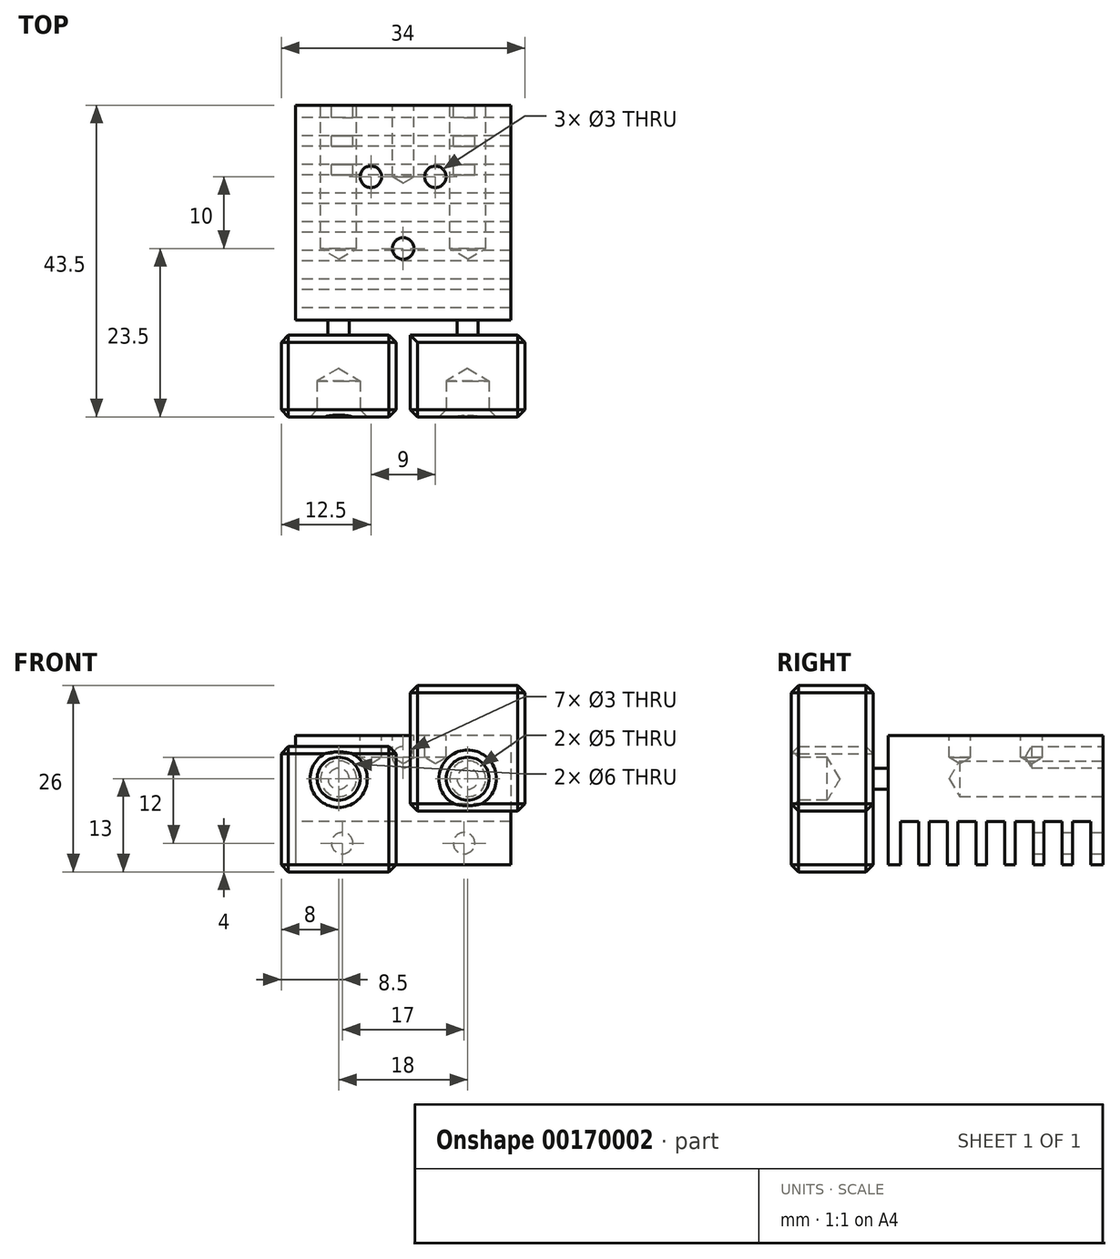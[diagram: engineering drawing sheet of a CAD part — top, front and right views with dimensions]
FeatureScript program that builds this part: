
annotation { "Feature Type Name" : "Feature", "Feature Type Description" : "" }
export const myFeature = defineFeature(function(context is Context, id is Id, definition is map)
    precondition{}
    {
        {
            var Q0;
            Q0=qCreatedBy(makeId("Top.planeOp"),FACE);
            var sketch = newSketch(context, id + "F0", { "sketchPlane" : qUnion([Q0])});
            skLineSegment(sketch, "E0.bottom", {"start": v(15, -15) * mm, "end": v(-15, -15) * mm});
            skLineSegment(sketch, "E0.top", {"start": v(15, 15) * mm, "end": v(-15, 15) * mm});
            skLineSegment(sketch, "E0.left", {"start": v(15, -15) * mm, "end": v(15, 15) * mm});
            skLineSegment(sketch, "E0.right", {"start": v(-15, -15) * mm, "end": v(-15, 15) * mm});
            skPoint(sketch, "E0.middle", {"position": v(0, 0) * mm});
            skSolve(sketch);
        }
        {
            var Q0;
            Q0=makeQuery(id+"F0.imprint","IMPRINT",FACE,{"disambiguationData":[TD([[makeQuery(id+"F0.imprint","IMPRINT",EDGE,{"derivedFrom":sQuery(id+"F0.wireOp",EDGE,"E0.bottom")}),-1.0]])]});
            extrude(context, id + "F6", {"entities" : qUnion([Q0]), "depth" : 18 * mm});
        }
        {
            var Q0;
            Q0=makeQuery(id+"F6.opExtrude","SWEPT_FACE",FACE,{"disambiguationData":[OSD([sQuery(id+"F0.wireOp",EDGE,"E0.top")])]});
            var sketch = newSketch(context, id + "F7", { "sketchPlane" : qUnion([Q0])});
            skPoint(sketch, "E1", {"position": v(-8.5, 3) * mm});
            skPoint(sketch, "E2", {"position": v(8.5, 3) * mm});
            skPoint(sketch, "E3", {"position": v(-9, 12) * mm});
            skPoint(sketch, "E4", {"position": v(9, 12) * mm});
            skPoint(sketch, "E5", {"position": v(0, 15) * mm});
            skSolve(sketch);
        }
        {
            var Q0;
            Q0=sQuery(id+"F7.wireOp",VERTEX,"E3");
            var Q1;
            Q1=sQuery(id+"F7.wireOp",VERTEX,"E4");
            var Q2;
            Q2=makeQuery(id+"F6.opExtrude","SWEPT_BODY",BODY,{"disambiguationData":[OSD([sQuery(id+"F0.wireOp",EDGE,"E0.bottom"),sQuery(id+"F0.wireOp",EDGE,"E0.top"),sQuery(id+"F0.wireOp",EDGE,"E0.left"),sQuery(id+"F0.wireOp",EDGE,"E0.right")])]});
            hole(context, id + "F1", {"style" : HoleStyle.SIMPLE, "endStyle" : HoleEndStyle.BLIND, "holeDiameter" : 5 * mm, "holeDepth" : 20 * mm, "locations" : qUnion([Q0, Q1]), "scope" : qUnion([Q2])});
        }
        {
            var Q0;
            Q0=makeQuery(id+"F6.opExtrude","CAP_FACE",FACE,{"disambiguationData":[OSD([sQuery(id+"F0.wireOp",EDGE,"E0.bottom"),sQuery(id+"F0.wireOp",EDGE,"E0.top"),sQuery(id+"F0.wireOp",EDGE,"E0.left"),sQuery(id+"F0.wireOp",EDGE,"E0.right")])],"isStart":true});
            var sketch = newSketch(context, id + "F8", { "sketchPlane" : qUnion([Q0])});
            skLineSegment(sketch, "E6.bottom", {"start": v(15, -13.25) * mm, "end": v(-15.01, -13.25) * mm});
            skLineSegment(sketch, "E6.top", {"start": v(15, -10.75) * mm, "end": v(-15.01, -10.75) * mm});
            skLineSegment(sketch, "E6.left", {"start": v(15, -13.25) * mm, "end": v(15, -10.75) * mm});
            skLineSegment(sketch, "E6.right", {"start": v(-15.01, -13.25) * mm, "end": v(-15.01, -10.75) * mm});
            skLineSegment(sketch, "E7.0.1.0", {"start": v(15, -9.25) * mm, "end": v(15, -6.75) * mm});
            skLineSegment(sketch, "E7.0.1.1", {"start": v(-15.01, -9.25) * mm, "end": v(-15.01, -6.75) * mm});
            skLineSegment(sketch, "E7.0.1.2", {"start": v(15, -9.25) * mm, "end": v(-15.01, -9.25) * mm});
            skLineSegment(sketch, "E7.0.1.3", {"start": v(15, -6.75) * mm, "end": v(-15.01, -6.75) * mm});
            skLineSegment(sketch, "E7.0.2.0", {"start": v(15, -5.25) * mm, "end": v(15, -2.75) * mm});
            skLineSegment(sketch, "E7.0.2.1", {"start": v(-15.01, -5.25) * mm, "end": v(-15.01, -2.75) * mm});
            skLineSegment(sketch, "E7.0.2.2", {"start": v(15, -5.25) * mm, "end": v(-15.01, -5.25) * mm});
            skLineSegment(sketch, "E7.0.2.3", {"start": v(15, -2.75) * mm, "end": v(-15.01, -2.75) * mm});
            skLineSegment(sketch, "E7.0.3.0", {"start": v(15, -1.25) * mm, "end": v(15, 1.25) * mm});
            skLineSegment(sketch, "E7.0.3.1", {"start": v(-15.01, -1.25) * mm, "end": v(-15.01, 1.25) * mm});
            skLineSegment(sketch, "E7.0.3.2", {"start": v(15, -1.25) * mm, "end": v(-15.01, -1.25) * mm});
            skLineSegment(sketch, "E7.0.3.3", {"start": v(15, 1.25) * mm, "end": v(-15.01, 1.25) * mm});
            skLineSegment(sketch, "E7.0.4.0", {"start": v(15, 2.75) * mm, "end": v(15, 5.25) * mm});
            skLineSegment(sketch, "E7.0.4.1", {"start": v(-15.01, 2.75) * mm, "end": v(-15.01, 5.25) * mm});
            skLineSegment(sketch, "E7.0.4.2", {"start": v(15, 2.75) * mm, "end": v(-15.01, 2.75) * mm});
            skLineSegment(sketch, "E7.0.4.3", {"start": v(15, 5.25) * mm, "end": v(-15.01, 5.25) * mm});
            skLineSegment(sketch, "E7.0.5.0", {"start": v(15, 6.75) * mm, "end": v(15, 9.25) * mm});
            skLineSegment(sketch, "E7.0.5.1", {"start": v(-15.01, 6.75) * mm, "end": v(-15.01, 9.25) * mm});
            skLineSegment(sketch, "E7.0.5.2", {"start": v(15, 6.75) * mm, "end": v(-15.01, 6.75) * mm});
            skLineSegment(sketch, "E7.0.5.3", {"start": v(15, 9.25) * mm, "end": v(-15.01, 9.25) * mm});
            skLineSegment(sketch, "E7.0.6.0", {"start": v(15, 10.75) * mm, "end": v(15, 13.25) * mm});
            skLineSegment(sketch, "E7.0.6.1", {"start": v(-15.01, 10.75) * mm, "end": v(-15.01, 13.25) * mm});
            skLineSegment(sketch, "E7.0.6.2", {"start": v(15, 10.75) * mm, "end": v(-15.01, 10.75) * mm});
            skLineSegment(sketch, "E7.0.6.3", {"start": v(15, 13.25) * mm, "end": v(-15.01, 13.25) * mm});
            skLineSegment(sketch, "E7.direction1", {"start": v(-15.01, -13.25) * mm, "end": v(9.99, -13.25) * mm, "construction": true});
            skLineSegment(sketch, "E7.direction2", {"start": v(-15.01, -13.25) * mm, "end": v(-15.01, -9.25) * mm, "construction": true});
            skSolve(sketch);
        }
        {
            var Q0;
            {var subQ0=sQuery(id+"F8.wireOp",EDGE,"E7.0.6.0");Q0=makeQuery(id+"F8.imprint","IMPRINT",FACE,{"disambiguationData":[TD([[makeQuery(id+"F8.imprint","IMPRINT",EDGE,{"derivedFrom":subQ0}),-1.0]])]});}
            var Q1;
            {var subQ0=sQuery(id+"F8.wireOp",EDGE,"E7.0.5.0");Q1=makeQuery(id+"F8.imprint","IMPRINT",FACE,{"disambiguationData":[TD([[makeQuery(id+"F8.imprint","IMPRINT",EDGE,{"derivedFrom":subQ0}),-1.0]])]});}
            var Q2;
            {var subQ0=sQuery(id+"F8.wireOp",EDGE,"E7.0.4.0");Q2=makeQuery(id+"F8.imprint","IMPRINT",FACE,{"disambiguationData":[TD([[makeQuery(id+"F8.imprint","IMPRINT",EDGE,{"derivedFrom":subQ0}),-1.0]])]});}
            var Q3;
            {var subQ0=sQuery(id+"F8.wireOp",EDGE,"E7.0.3.0");Q3=makeQuery(id+"F8.imprint","IMPRINT",FACE,{"disambiguationData":[TD([[makeQuery(id+"F8.imprint","IMPRINT",EDGE,{"derivedFrom":subQ0}),-1.0]])]});}
            var Q4;
            {var subQ0=sQuery(id+"F8.wireOp",EDGE,"E7.0.2.0");Q4=makeQuery(id+"F8.imprint","IMPRINT",FACE,{"disambiguationData":[TD([[makeQuery(id+"F8.imprint","IMPRINT",EDGE,{"derivedFrom":subQ0}),-1.0]])]});}
            var Q5;
            {var subQ0=sQuery(id+"F8.wireOp",EDGE,"E7.0.1.0");Q5=makeQuery(id+"F8.imprint","IMPRINT",FACE,{"disambiguationData":[TD([[makeQuery(id+"F8.imprint","IMPRINT",EDGE,{"derivedFrom":subQ0}),-1.0]])]});}
            var Q6;
            {var subQ0=sQuery(id+"F8.wireOp",EDGE,"E6.left");Q6=makeQuery(id+"F8.imprint","IMPRINT",FACE,{"disambiguationData":[TD([[makeQuery(id+"F8.imprint","IMPRINT",EDGE,{"derivedFrom":subQ0}),-1.0]])]});}
            extrude(context, id + "F9", {"entities" : qUnion([Q0, Q1, Q2, Q3, Q4, Q5, Q6]), "operationType" : NewBodyOperationType.REMOVE, "oppositeDirection" : true, "depth" : 6 * mm});
        }
        {
            var Q0;
            Q0=makeQuery(id+"F6.opExtrude","CAP_FACE",FACE,{"disambiguationData":[OSD([sQuery(id+"F0.wireOp",EDGE,"E0.bottom"),sQuery(id+"F0.wireOp",EDGE,"E0.top"),sQuery(id+"F0.wireOp",EDGE,"E0.left"),sQuery(id+"F0.wireOp",EDGE,"E0.right")])],"isStart":false});
            var sketch = newSketch(context, id + "F2", { "sketchPlane" : qUnion([Q0])});
            skPoint(sketch, "E8", {"position": v(-4.5, 5) * mm});
            skPoint(sketch, "E9", {"position": v(4.5, 5) * mm});
            skPoint(sketch, "E10", {"position": v(0, -5) * mm});
            skSolve(sketch);
        }
        {
            var Q0;
            Q0=sQuery(id+"F2.wireOp",VERTEX,"E9");
            var Q1;
            Q1=sQuery(id+"F2.wireOp",VERTEX,"E8");
            var Q2;
            Q2=sQuery(id+"F2.wireOp",VERTEX,"E10");
            var Q3;
            Q3=makeQuery(id+"F6.opExtrude","SWEPT_BODY",BODY,{"disambiguationData":[OSD([sQuery(id+"F0.wireOp",EDGE,"E0.bottom"),sQuery(id+"F0.wireOp",EDGE,"E0.top"),sQuery(id+"F0.wireOp",EDGE,"E0.left"),sQuery(id+"F0.wireOp",EDGE,"E0.right")])]});
            hole(context, id + "F10", {"style" : HoleStyle.SIMPLE, "endStyle" : HoleEndStyle.BLIND, "holeDiameter" : 3 * mm, "holeDepth" : 3 * mm, "locations" : qUnion([Q0, Q1, Q2]), "scope" : qUnion([Q3])});
        }
        {
            var Q0;
            Q0=sQuery(id+"F7.wireOp",VERTEX,"E2");
            var Q1;
            Q1=sQuery(id+"F7.wireOp",VERTEX,"E1");
            var Q2;
            Q2=sQuery(id+"F7.wireOp",VERTEX,"E5");
            var Q3;
            Q3=makeQuery(id+"F6.opExtrude","SWEPT_BODY",BODY,{"disambiguationData":[OSD([sQuery(id+"F0.wireOp",EDGE,"E0.bottom"),sQuery(id+"F0.wireOp",EDGE,"E0.top"),sQuery(id+"F0.wireOp",EDGE,"E0.left"),sQuery(id+"F0.wireOp",EDGE,"E0.right")])]});
            hole(context, id + "F11", {"style" : HoleStyle.SIMPLE, "endStyle" : HoleEndStyle.BLIND, "holeDiameter" : 3 * mm, "holeDepth" : 10 * mm, "locations" : qUnion([Q0, Q1, Q2]), "scope" : qUnion([Q3])});
        }
        {
            var Q0;
            Q0=makeQuery(id+"F6.opExtrude","SWEPT_FACE",FACE,{"disambiguationData":[OSD([sQuery(id+"F0.wireOp",EDGE,"E0.bottom")])]});
            var sketch = newSketch(context, id + "F3", { "sketchPlane" : qUnion([Q0])});
            skCircle(sketch, "E11", {"center": v(9, 12) * mm, "radius": 1.48 * mm});
            skCircle(sketch, "E12", {"center": v(-9, 12) * mm, "radius": 1.48 * mm});
            skSolve(sketch);
        }
        {
            var Q0;
            Q0=makeQuery(id+"F3.imprint","IMPRINT",FACE,{"disambiguationData":[TD([[makeQuery(id+"F3.imprint","IMPRINT",EDGE,{"derivedFrom":sQuery(id+"F3.wireOp",EDGE,"E12")}),1.0]])]});
            var Q1;
            Q1=makeQuery(id+"F3.imprint","IMPRINT",FACE,{"disambiguationData":[TD([[makeQuery(id+"F3.imprint","IMPRINT",EDGE,{"derivedFrom":sQuery(id+"F3.wireOp",EDGE,"E11")}),1.0]])]});
            extrude(context, id + "F4", {"entities" : qUnion([Q0, Q1]), "operationType" : NewBodyOperationType.ADD, "depth" : 2.1 * mm});
        }
        {
            var Q0;
            Q0=makeQuery(id+"F4.opExtrude","CAP_FACE",FACE,{"disambiguationData":[OSD([sQuery(id+"F3.wireOp",EDGE,"E11")])],"isStart":false});
            var sketch = newSketch(context, id + "F12", { "sketchPlane" : qUnion([Q0])});
            skLineSegment(sketch, "E13.bottom", {"start": v(1, 25) * mm, "end": v(17, 25) * mm});
            skLineSegment(sketch, "E13.top", {"start": v(1, 7.5) * mm, "end": v(17, 7.5) * mm});
            skLineSegment(sketch, "E13.left", {"start": v(1, 25) * mm, "end": v(1, 7.5) * mm});
            skLineSegment(sketch, "E13.right", {"start": v(17, 25) * mm, "end": v(17, 7.5) * mm});
            skPoint(sketch, "E14", {"position": v(9, 12) * mm});
            skSolve(sketch);
        }
        {
            var Q0;
            Q0=makeQuery(id+"F4.opExtrude","CAP_FACE",FACE,{"disambiguationData":[OSD([sQuery(id+"F3.wireOp",EDGE,"E12")])],"isStart":false});
            var sketch = newSketch(context, id + "F13", { "sketchPlane" : qUnion([Q0])});
            skPoint(sketch, "E15", {"position": v(-9, 12) * mm});
            skLineSegment(sketch, "E16.bottom", {"start": v(-17, 16.5) * mm, "end": v(-1, 16.5) * mm});
            skLineSegment(sketch, "E16.top", {"start": v(-17, -1) * mm, "end": v(-1, -1) * mm});
            skLineSegment(sketch, "E16.left", {"start": v(-17, 16.5) * mm, "end": v(-17, -1) * mm});
            skLineSegment(sketch, "E16.right", {"start": v(-1, 16.5) * mm, "end": v(-1, -1) * mm});
            skSolve(sketch);
        }
        {
            var Q0;
            Q0=qSketchRegion(id+"F13",true);
            var Q1;
            Q1=qSketchRegion(id+"F12",true);
            extrude(context, id + "F14", {"entities" : qUnion([Q0, Q1]), "operationType" : NewBodyOperationType.ADD, "depth" : 11.4 * mm});
        }
        {
            var Q0;
            Q0=makeQuery(id+"F14.opExtrude","CAP_FACE",FACE,{"disambiguationData":[OSD([sQuery(id+"F12.wireOp",EDGE,"E13.bottom"),sQuery(id+"F12.wireOp",EDGE,"E13.top"),sQuery(id+"F12.wireOp",EDGE,"E13.left"),sQuery(id+"F12.wireOp",EDGE,"E13.right")])],"isStart":false});
            var sketch = newSketch(context, id + "F15", { "sketchPlane" : qUnion([Q0])});
            skPoint(sketch, "E17", {"position": v(9, 12) * mm});
            skPoint(sketch, "E17.positionSnap0", {"position": v(9, 7.5) * mm});
            skSolve(sketch);
        }
        {
            var Q0;
            Q0=makeQuery(id+"F14.opExtrude","CAP_FACE",FACE,{"disambiguationData":[OSD([sQuery(id+"F13.wireOp",EDGE,"E16.bottom"),sQuery(id+"F13.wireOp",EDGE,"E16.top"),sQuery(id+"F13.wireOp",EDGE,"E16.left"),sQuery(id+"F13.wireOp",EDGE,"E16.right")])],"isStart":false});
            var sketch = newSketch(context, id + "F16", { "sketchPlane" : qUnion([Q0])});
            skPoint(sketch, "E18", {"position": v(-9, 12) * mm});
            skPoint(sketch, "E18.positionSnap0", {"position": v(-9, 16.5) * mm});
            skSolve(sketch);
        }
        {
            var Q0;
            Q0=sQuery(id+"F16.wireOp",VERTEX,"E18");
            var Q1;
            Q1=sQuery(id+"F15.wireOp",VERTEX,"E17");
            var Q2;
            Q2=makeQuery(id+"F6.opExtrude","SWEPT_BODY",BODY,{"disambiguationData":[OSD([sQuery(id+"F0.wireOp",EDGE,"E0.bottom"),sQuery(id+"F0.wireOp",EDGE,"E0.top"),sQuery(id+"F0.wireOp",EDGE,"E0.left"),sQuery(id+"F0.wireOp",EDGE,"E0.right")])]});
            hole(context, id + "F5", {"style" : HoleStyle.SIMPLE, "endStyle" : HoleEndStyle.BLIND, "holeDiameter" : 6 * mm, "holeDepth" : 5 * mm, "locations" : qUnion([Q0, Q1]), "scope" : qUnion([Q2])});
        }
        {
            var Q0;
            Q0=makeQuery(id+"F14.opExtrude","CAP_EDGE",EDGE,{"disambiguationData":[OSD([sQuery(id+"F13.wireOp",EDGE,"E16.left")])],"isStart":false});
            var Q1;
            Q1=makeQuery(id+"F14.opExtrude","SWEPT_FACE",FACE,{"disambiguationData":[OSD([sQuery(id+"F13.wireOp",EDGE,"E16.top")])]});
            var Q2;
            Q2=makeQuery(id+"F14.opExtrude","SWEPT_FACE",FACE,{"disambiguationData":[OSD([sQuery(id+"F13.wireOp",EDGE,"E16.left")])]});
            var Q3;
            Q3=makeQuery(id+"F14.opExtrude","SWEPT_FACE",FACE,{"disambiguationData":[OSD([sQuery(id+"F13.wireOp",EDGE,"E16.bottom")])]});
            var Q4;
            Q4=makeQuery(id+"F14.opExtrude","SWEPT_FACE",FACE,{"disambiguationData":[OSD([sQuery(id+"F12.wireOp",EDGE,"E13.bottom")])]});
            var Q5;
            Q5=makeQuery(id+"F5.hole-1.boolean.opBoolean","COPY",EDGE,{"derivedFrom":makeQuery(id+"F5.hole-1.opRevolve","SWEPT_EDGE",EDGE,{"disambiguationData":[OSD([sQuery(id+"F5.hole-1.sketch.wireOp",EDGE,"core_line_2"),sQuery(id+"F5.hole-1.sketch.wireOp",EDGE,"core_line_3")])]})});
            var Q6;
            Q6=makeQuery(id+"F14.opExtrude","CAP_FACE",FACE,{"disambiguationData":[OSD([sQuery(id+"F12.wireOp",EDGE,"E13.bottom"),sQuery(id+"F12.wireOp",EDGE,"E13.top"),sQuery(id+"F12.wireOp",EDGE,"E13.left"),sQuery(id+"F12.wireOp",EDGE,"E13.right")])],"isStart":false});
            var Q7;
            Q7=makeQuery(id+"F14.opExtrude","CAP_FACE",FACE,{"disambiguationData":[OSD([sQuery(id+"F13.wireOp",EDGE,"E16.bottom"),sQuery(id+"F13.wireOp",EDGE,"E16.top"),sQuery(id+"F13.wireOp",EDGE,"E16.left"),sQuery(id+"F13.wireOp",EDGE,"E16.right")])],"isStart":false});
            var Q8;
            Q8=makeQuery(id+"F14.opExtrude","SWEPT_FACE",FACE,{"disambiguationData":[OSD([sQuery(id+"F12.wireOp",EDGE,"E13.top")])]});
            var Q9;
            Q9=makeQuery(id+"F14.opExtrude","SWEPT_FACE",FACE,{"disambiguationData":[OSD([sQuery(id+"F12.wireOp",EDGE,"E13.right")])]});
            var Q10;
            Q10=makeQuery(id+"F14.opExtrude","SWEPT_FACE",FACE,{"disambiguationData":[OSD([sQuery(id+"F13.wireOp",EDGE,"E16.right")])]});
            chamfer(context, id + "F17", {"entities" : qUnion([Q0, Q1, Q2, Q3, Q4, Q5, Q6, Q7, Q8, Q9, Q10]), "width" : 1 * mm, "tangentPropagation" : true});
        }
    });
